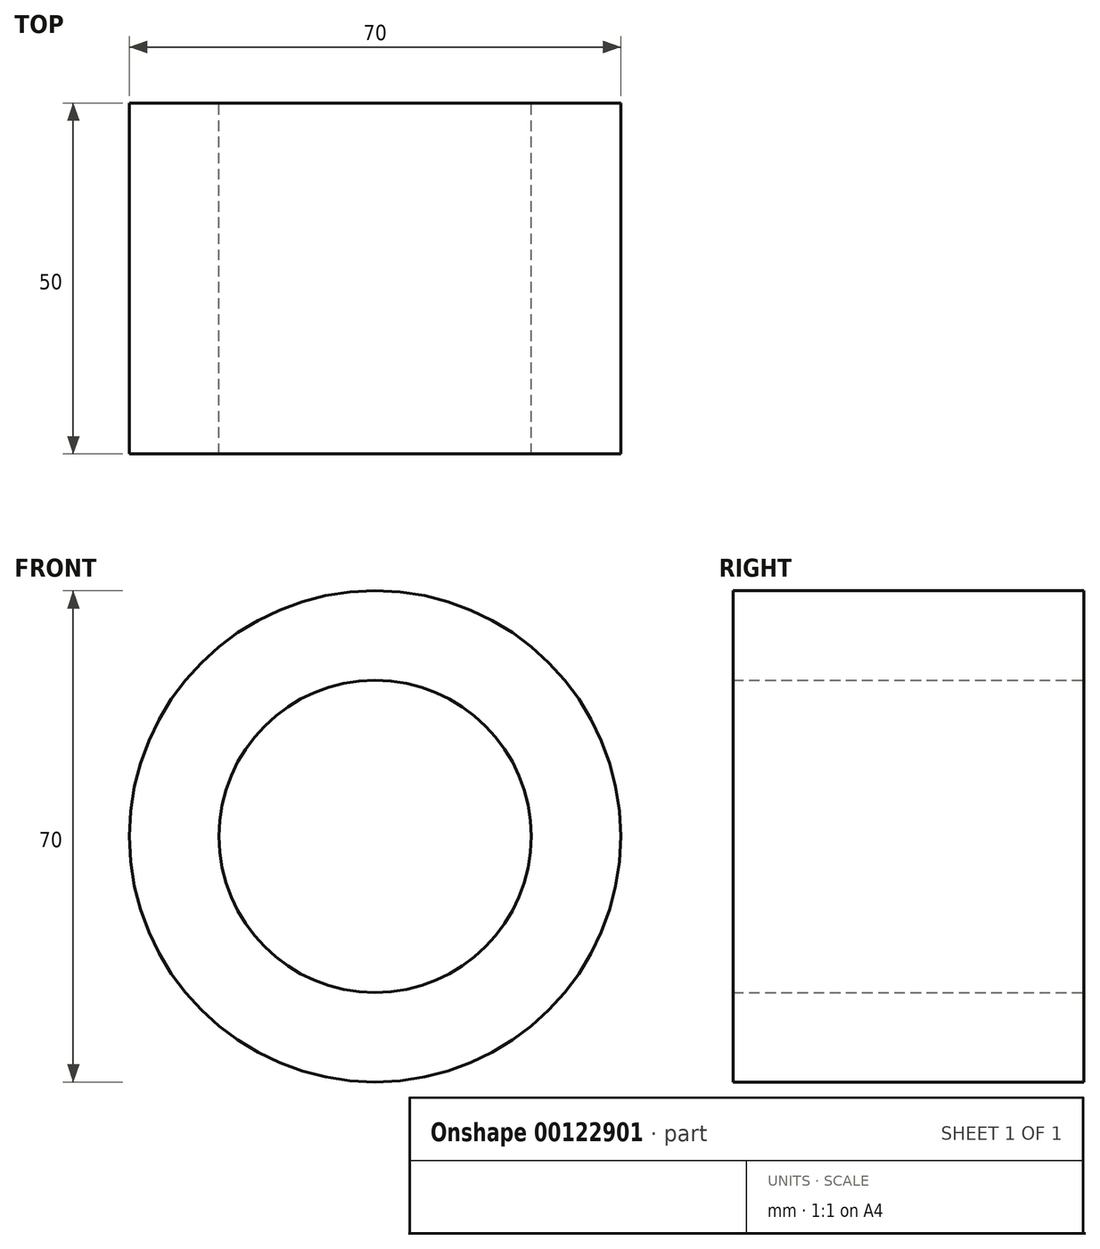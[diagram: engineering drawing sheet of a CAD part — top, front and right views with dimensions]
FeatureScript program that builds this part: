
annotation { "Feature Type Name" : "Feature", "Feature Type Description" : "" }
export const myFeature = defineFeature(function(context is Context, id is Id, definition is map)
    precondition{}
    {
        {
            var Q0;
            Q0=qCreatedBy(makeId("Front.planeOp"),FACE);
            var sketch = newSketch(context, id + "F0", { "sketchPlane" : qUnion([Q0])});
            skCircle(sketch, "E0", {"center": v(-29.25, 20.38) * mm, "radius": 35 * mm});
            skCircle(sketch, "E1", {"center": v(-29.25, 20.38) * mm, "radius": 22.25 * mm});
            skSolve(sketch);
        }
        {
            var Q0;
            Q0=makeQuery(id+"F0.imprint","IMPRINT",FACE,{"disambiguationData":[TD([[makeQuery(id+"F0.imprint","IMPRINT",EDGE,{"derivedFrom":sQuery(id+"F0.wireOp",EDGE,"E0")}),1.0]])]});
            extrude(context, id + "F1", {"entities" : qUnion([Q0]), "depth" : 50 * mm});
        }
    });
